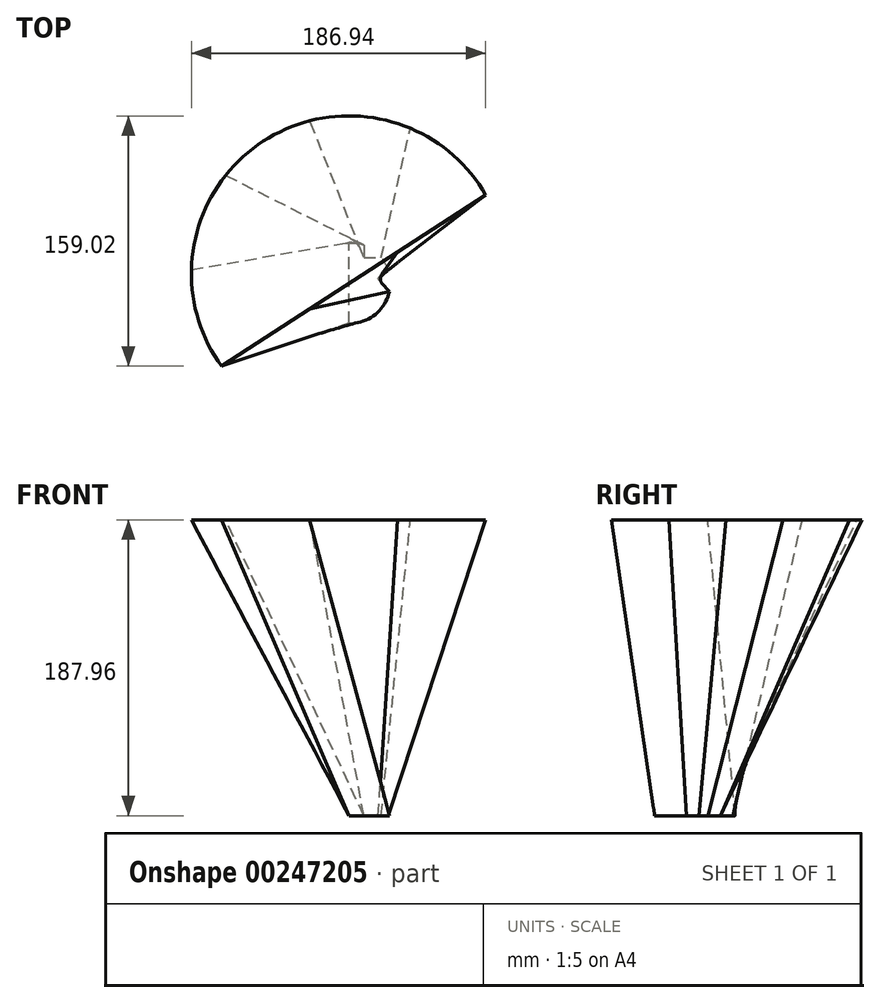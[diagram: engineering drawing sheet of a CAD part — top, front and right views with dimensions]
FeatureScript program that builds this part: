
annotation { "Feature Type Name" : "Feature", "Feature Type Description" : "" }
export const myFeature = defineFeature(function(context is Context, id is Id, definition is map)
    precondition{}
    {
        {
            var Q0;
            Q0=qCreatedBy(makeId("Top.planeOp"),FACE);
            var sketch = newSketch(context, id + "F0", { "sketchPlane" : qUnion([Q0])});
            skLineSegment(sketch, "E0", {"start": v(0, 0) * mm, "end": v(0, 51.09) * mm});
            skArc(sketch, "E1", {"start": v(0, 0) * mm, "mid": v(16.48, 5.49) * mm, "end": v(25.64, 20.25) * mm});
            skLineSegment(sketch, "E2", {"start": v(24.8, 33.86) * mm, "end": v(18.48, 28.1) * mm});
            skLineSegment(sketch, "E3", {"start": v(18.48, 28.1) * mm, "end": v(25.64, 20.25) * mm});
            skArc(sketch, "E4.trimOffspring", {"start": v(24.8, 33.86) * mm, "mid": v(22.96, 38) * mm, "end": v(20.4, 41.74) * mm});
            skLineSegment(sketch, "E5.top", {"start": v(9.37, 41.74) * mm, "end": v(20.4, 41.74) * mm});
            skLineSegment(sketch, "E5.left", {"start": v(9.37, 49.56) * mm, "end": v(9.37, 41.74) * mm});
            skArc(sketch, "E6.trimOffspring", {"start": v(9.37, 49.56) * mm, "mid": v(4.75, 50.76) * mm, "end": v(0, 51.09) * mm});
            skSolve(sketch);
        }
        {
            var Q0;
            Q0=qCreatedBy(makeId("Top.planeOp"),FACE);
            cPlane(context, id + "F1", {"entities" : qUnion([Q0]), "cplaneType" : CPlaneType.OFFSET, "offset" : 187.96 * mm, "width" : 152.4 * mm, "height" : 152.4 * mm});
        }
        {
            var Q0;
            Q0=qCreatedBy(id+"F1.planeOp",FACE);
            var sketch = newSketch(context, id + "F2", { "sketchPlane" : qUnion([Q0])});
            skArc(sketch, "E7", {"start": v(86.79, 81.52) * mm, "mid": v(-54.5, 115.56) * mm, "end": v(-81.02, -27.33) * mm});
            skLineSegment(sketch, "E8", {"start": v(86.79, 81.52) * mm, "end": v(-81.02, -27.33) * mm});
            skSolve(sketch);
        }
        {
            var Q0;
            Q0=makeQuery(id+"F0.imprint","IMPRINT",FACE,{"disambiguationData":[TD([[makeQuery(id+"F0.imprint","IMPRINT",EDGE,{"derivedFrom":sQuery(id+"F0.wireOp",EDGE,"E0")}),-1.0]])]});
            var Q1;
            Q1=makeQuery(id+"F2.imprint","IMPRINT",FACE,{"disambiguationData":[TD([[makeQuery(id+"F2.imprint","IMPRINT",EDGE,{"derivedFrom":sQuery(id+"F2.wireOp",EDGE,"E7")}),1.0]])]});
            loft(context, id + "F3", {"sheetProfilesArray" : [{ "sheetProfileEntities" : qUnion([Q0]) }, { "sheetProfileEntities" : qUnion([Q1]) }]});
        }
    });
